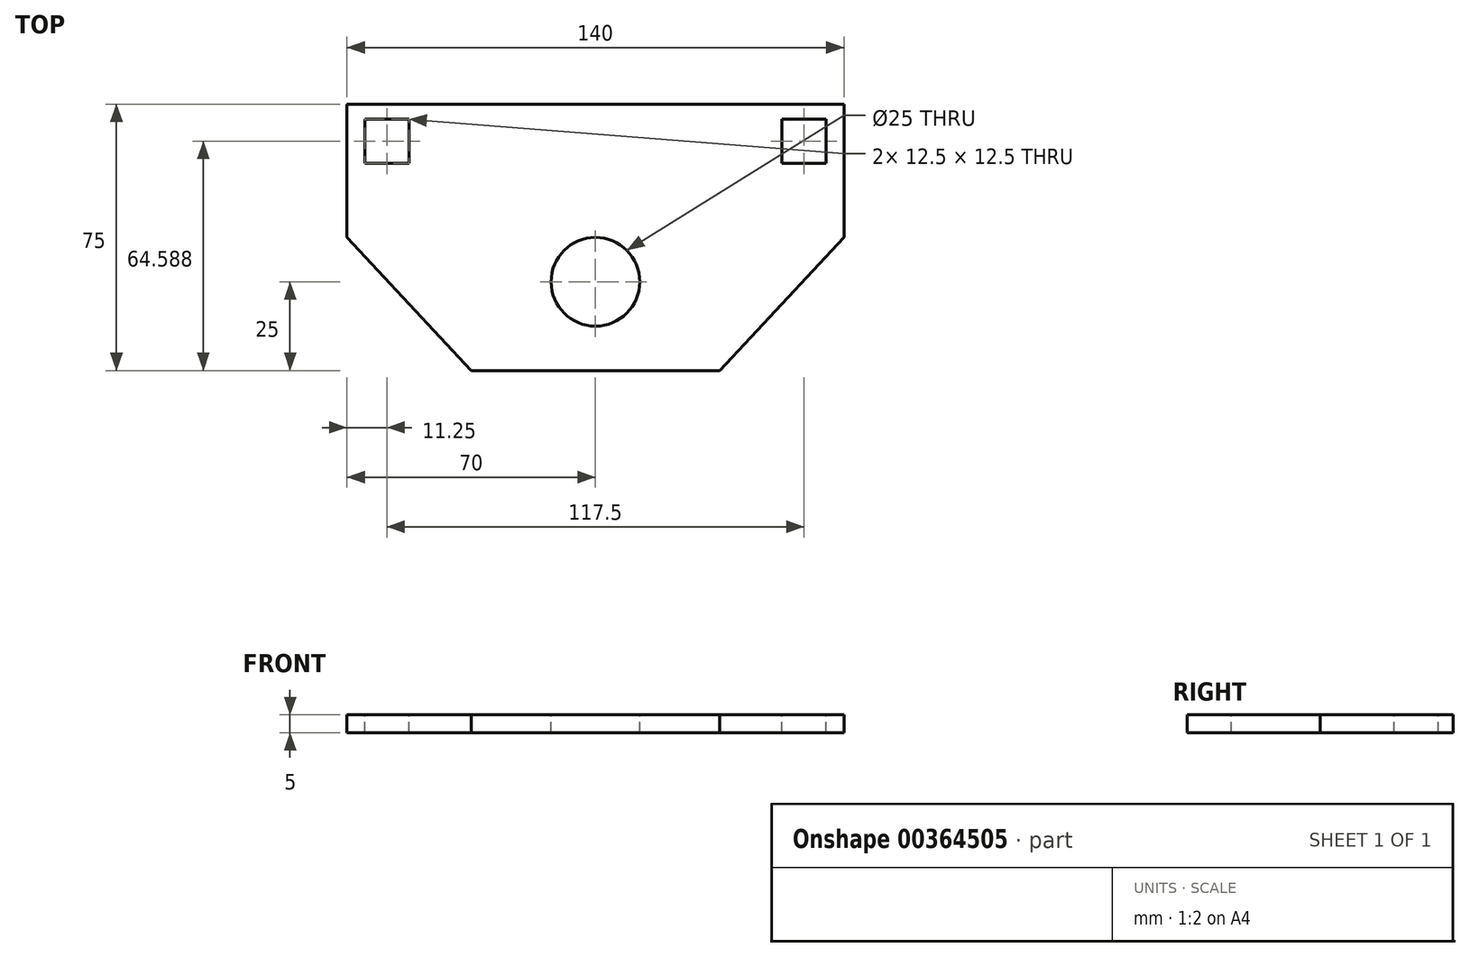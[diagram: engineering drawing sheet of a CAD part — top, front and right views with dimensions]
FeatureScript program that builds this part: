
annotation { "Feature Type Name" : "Feature", "Feature Type Description" : "" }
export const myFeature = defineFeature(function(context is Context, id is Id, definition is map)
    precondition{}
    {
        {
            var Q0;
            Q0=qCreatedBy(makeId("Top.planeOp"),FACE);
            var sketch = newSketch(context, id + "F0", { "sketchPlane" : qUnion([Q0])});
            skLineSegment(sketch, "E0.bottom", {"start": v(-67.77, 45.9) * mm, "end": v(72.23, 45.9) * mm});
            skLineSegment(sketch, "E0.top", {"start": v(-67.77, -29.1) * mm, "end": v(72.23, -29.1) * mm});
            skLineSegment(sketch, "E0.left", {"start": v(-67.77, 45.9) * mm, "end": v(-67.77, -29.1) * mm});
            skLineSegment(sketch, "E0.right", {"start": v(72.23, 45.9) * mm, "end": v(72.23, -29.1) * mm});
            skSolve(sketch);
        }
        {
            var Q0;
            Q0=makeQuery(id+"F0.imprint","IMPRINT",FACE,{"disambiguationData":[TD([[makeQuery(id+"F0.imprint","IMPRINT",EDGE,{"derivedFrom":sQuery(id+"F0.wireOp",EDGE,"E0.bottom")}),-1.0]])]});
            extrude(context, id + "F1", {"entities" : qUnion([Q0]), "depth" : 5 * mm});
        }
        {
            var Q0;
            Q0=makeQuery(id+"F1.opExtrude","CAP_FACE",FACE,{"disambiguationData":[OSD([sQuery(id+"F0.wireOp",EDGE,"E0.bottom"),sQuery(id+"F0.wireOp",EDGE,"E0.top"),sQuery(id+"F0.wireOp",EDGE,"E0.left"),sQuery(id+"F0.wireOp",EDGE,"E0.right")])],"isStart":false});
            var sketch = newSketch(context, id + "F2", { "sketchPlane" : qUnion([Q0])});
            skLineSegment(sketch, "E1.bottom", {"start": v(-62.77, 41.75) * mm, "end": v(-50.27, 41.75) * mm});
            skLineSegment(sketch, "E1.top", {"start": v(-62.77, 29.25) * mm, "end": v(-50.27, 29.25) * mm});
            skLineSegment(sketch, "E1.left", {"start": v(-62.77, 41.75) * mm, "end": v(-62.77, 29.25) * mm});
            skLineSegment(sketch, "E1.right", {"start": v(-50.27, 41.75) * mm, "end": v(-50.27, 29.25) * mm});
            skLineSegment(sketch, "E2", {"start": v(2.23, -29.1) * mm, "end": v(2.23, 45.9) * mm, "construction": true});
            skLineSegment(sketch, "E3.MirrorCS", {"start": v(54.73, 41.75) * mm, "end": v(54.73, 29.25) * mm});
            skLineSegment(sketch, "E4.MirrorCS", {"start": v(67.23, 41.75) * mm, "end": v(67.23, 29.25) * mm});
            skLineSegment(sketch, "E5.MirrorCS", {"start": v(67.23, 29.25) * mm, "end": v(54.73, 29.25) * mm});
            skLineSegment(sketch, "E6.MirrorCS", {"start": v(67.23, 41.75) * mm, "end": v(54.73, 41.75) * mm});
            skSolve(sketch);
        }
        {
            var Q0;
            Q0=makeQuery(id+"F2.imprint","IMPRINT",FACE,{"disambiguationData":[TD([[makeQuery(id+"F2.imprint","IMPRINT",EDGE,{"derivedFrom":sQuery(id+"F2.wireOp",EDGE,"E1.bottom")}),-1.0]])]});
            var Q1;
            Q1=makeQuery(id+"F2.imprint","IMPRINT",FACE,{"disambiguationData":[TD([[makeQuery(id+"F2.imprint","IMPRINT",EDGE,{"derivedFrom":sQuery(id+"F2.wireOp",EDGE,"E3.MirrorCS")}),1.0]])]});
            extrude(context, id + "F3", {"entities" : qUnion([Q0, Q1]), "operationType" : NewBodyOperationType.REMOVE, "oppositeDirection" : true, "depth" : 25 * mm});
        }
        {
            var Q0;
            Q0=makeQuery(id+"F1.opExtrude","CAP_FACE",FACE,{"disambiguationData":[OSD([sQuery(id+"F0.wireOp",EDGE,"E0.bottom"),sQuery(id+"F0.wireOp",EDGE,"E0.top"),sQuery(id+"F0.wireOp",EDGE,"E0.left"),sQuery(id+"F0.wireOp",EDGE,"E0.right")])],"isStart":false});
            var sketch = newSketch(context, id + "F4", { "sketchPlane" : qUnion([Q0])});
            skLineSegment(sketch, "E7", {"start": v(2.23, 45.9) * mm, "end": v(2.23, -29.1) * mm, "construction": true});
            skCircle(sketch, "E8", {"center": v(2.23, -4.1) * mm, "radius": 12.5 * mm});
            skSolve(sketch);
        }
        {
            var Q0;
            Q0=makeQuery(id+"F4.imprint","IMPRINT",FACE,{"disambiguationData":[TD([[makeQuery(id+"F4.imprint","IMPRINT",EDGE,{"derivedFrom":sQuery(id+"F4.wireOp",EDGE,"E8")}),1.0]])]});
            extrude(context, id + "F5", {"entities" : qUnion([Q0]), "operationType" : NewBodyOperationType.REMOVE, "oppositeDirection" : true, "depth" : 25 * mm});
        }
        {
            var Q0;
            Q0=makeQuery(id+"F1.opExtrude","CAP_FACE",FACE,{"disambiguationData":[OSD([sQuery(id+"F0.wireOp",EDGE,"E0.bottom"),sQuery(id+"F0.wireOp",EDGE,"E0.top"),sQuery(id+"F0.wireOp",EDGE,"E0.left"),sQuery(id+"F0.wireOp",EDGE,"E0.right")])],"isStart":false});
            var sketch = newSketch(context, id + "F6", { "sketchPlane" : qUnion([Q0])});
            skLineSegment(sketch, "E9", {"start": v(-67.77, 8.4) * mm, "end": v(-32.77, -29.1) * mm});
            skLineSegment(sketch, "E10", {"start": v(-32.77, -29.1) * mm, "end": v(-67.77, -29.1) * mm});
            skLineSegment(sketch, "E11", {"start": v(-67.77, -29.1) * mm, "end": v(-67.77, 8.4) * mm});
            skLineSegment(sketch, "E12", {"start": v(2.23, 45.9) * mm, "end": v(2.23, -4.1) * mm, "construction": true});
            skLineSegment(sketch, "E13.MirrorCS", {"start": v(72.23, 8.4) * mm, "end": v(37.23, -29.1) * mm});
            skLineSegment(sketch, "E14.MirrorCS", {"start": v(72.23, -29.1) * mm, "end": v(72.23, 8.4) * mm});
            skLineSegment(sketch, "E15.MirrorCS", {"start": v(37.23, -29.1) * mm, "end": v(72.23, -29.1) * mm});
            skSolve(sketch);
        }
        {
            var Q0;
            Q0=qSketchRegion(id+"F6",true);
            extrude(context, id + "F7", {"entities" : qUnion([Q0]), "operationType" : NewBodyOperationType.REMOVE, "oppositeDirection" : true, "depth" : 25 * mm});
        }
    });
